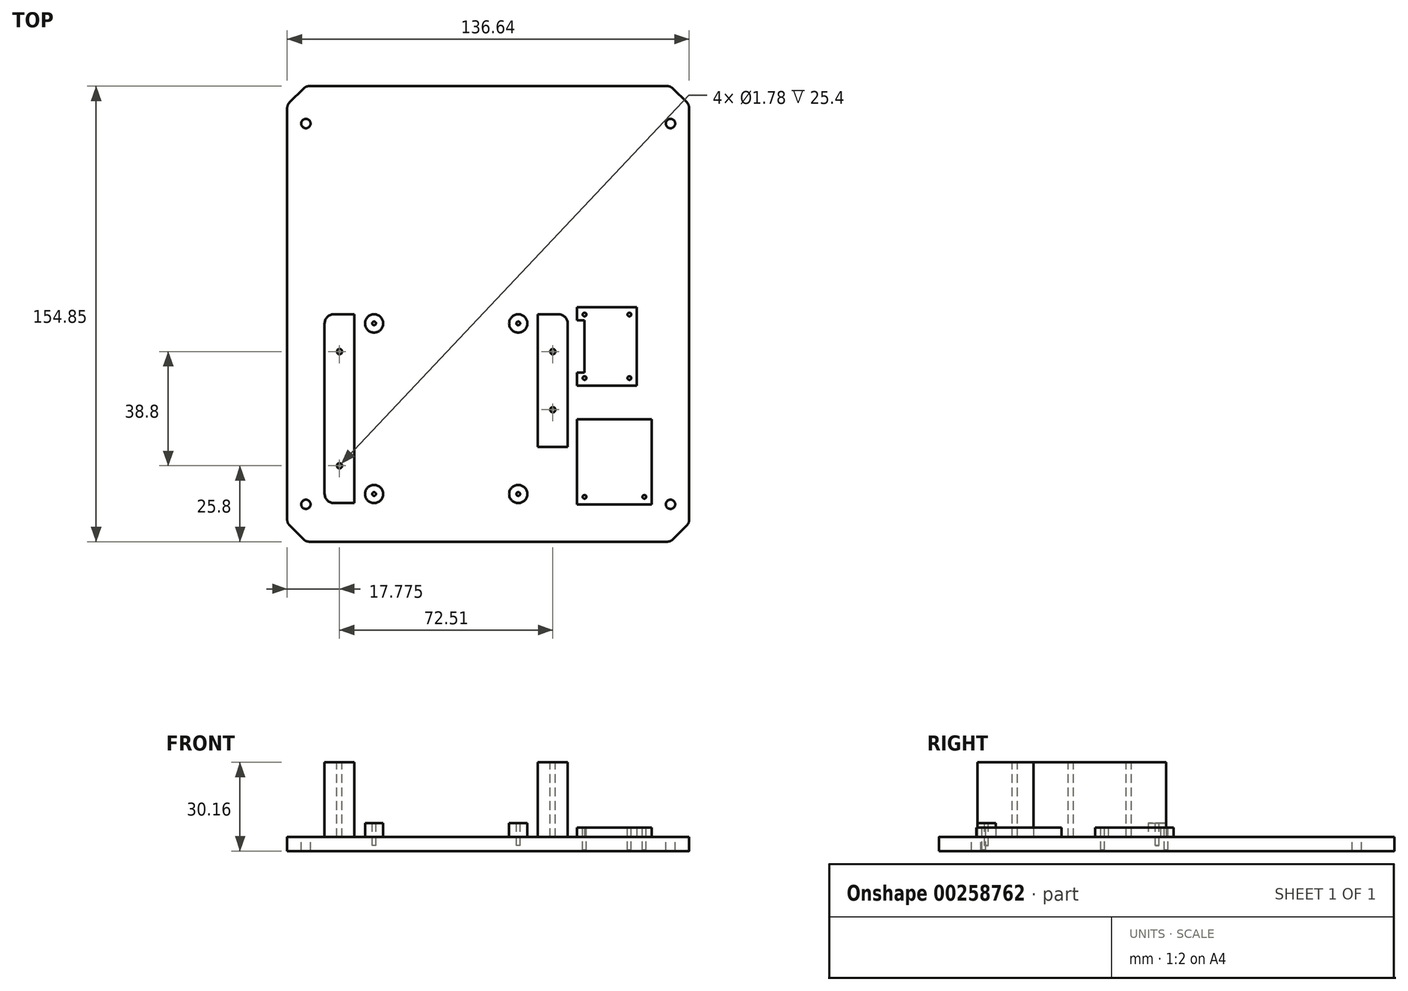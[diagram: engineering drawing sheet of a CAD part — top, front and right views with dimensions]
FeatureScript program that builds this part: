
annotation { "Feature Type Name" : "Feature", "Feature Type Description" : "" }
export const myFeature = defineFeature(function(context is Context, id is Id, definition is map)
    precondition{}
    {
        {
            var Q0;
            Q0=qCreatedBy(makeId("Top.planeOp"),FACE);
            var sketch = newSketch(context, id + "F0", { "sketchPlane" : qUnion([Q0])});
            skLineSegment(sketch, "E0.bottom", {"start": v(-25, 46.5) * mm, "end": v(25, 46.5) * mm});
            skLineSegment(sketch, "E0.top", {"start": v(-25, -38.5) * mm, "end": v(25, -38.5) * mm});
            skLineSegment(sketch, "E0.left", {"start": v(-28, 43.5) * mm, "end": v(-28, -35.5) * mm});
            skLineSegment(sketch, "E0.right", {"start": v(28, 43.5) * mm, "end": v(28, -35.5) * mm});
            skCircle(sketch, "E1", {"center": v(-24.5, -35) * mm, "radius": 3.1 * mm});
            skCircle(sketch, "E2", {"center": v(24.5, -35) * mm, "radius": 3.1 * mm});
            skCircle(sketch, "E3", {"center": v(24.5, 23) * mm, "radius": 3.1 * mm});
            skCircle(sketch, "E4", {"center": v(-24.5, 23) * mm, "radius": 3.1 * mm});
            skCircle(sketch, "E5", {"center": v(-24.5, 23) * mm, "radius": 1.38 * mm});
            skCircle(sketch, "E6", {"center": v(24.5, 23) * mm, "radius": 1.38 * mm});
            skCircle(sketch, "E7", {"center": v(24.5, -35) * mm, "radius": 1.38 * mm});
            skCircle(sketch, "E8", {"center": v(-24.5, -35) * mm, "radius": 1.38 * mm});
            skPoint(sketch, "E9.visualSharp", {"position": v(-28, 46.5) * mm});
            skArc(sketch, "E9.filletArc", {"start": v(-25, 46.5) * mm, "mid": v(-27.12, 45.62) * mm, "end": v(-28, 43.5) * mm});
            skPoint(sketch, "E10.visualSharp", {"position": v(28, 46.5) * mm});
            skArc(sketch, "E10.filletArc", {"start": v(28, 43.5) * mm, "mid": v(27.12, 45.62) * mm, "end": v(25, 46.5) * mm});
            skPoint(sketch, "E11.visualSharp", {"position": v(-28, -38.5) * mm});
            skArc(sketch, "E11.filletArc", {"start": v(-28, -35.5) * mm, "mid": v(-27.12, -37.62) * mm, "end": v(-25, -38.5) * mm});
            skPoint(sketch, "E12.visualSharp", {"position": v(28, -38.5) * mm});
            skArc(sketch, "E12.filletArc", {"start": v(25, -38.5) * mm, "mid": v(27.12, -37.62) * mm, "end": v(28, -35.5) * mm});
            skSolve(sketch);
        }
        {
            var Q0;
            Q0=qCreatedBy(makeId("Top.planeOp"),FACE);
            var sketch = newSketch(context, id + "F1", { "sketchPlane" : qUnion([Q0])});
            skLineSegment(sketch, "E13.top", {"start": v(-38.16, -38.1) * mm, "end": v(-34.35, -38.1) * mm});
            skLineSegment(sketch, "E13.left", {"start": v(-41.33, 22.92) * mm, "end": v(-41.33, -34.92) * mm});
            skLineSegment(sketch, "E13.right", {"start": v(-31.17, 22.92) * mm, "end": v(-31.17, -34.92) * mm});
            skLineSegment(sketch, "E14.left", {"start": v(31.18, 22.92) * mm, "end": v(31.18, -19.05) * mm});
            skLineSegment(sketch, "E14.right", {"start": v(41.33, 22.92) * mm, "end": v(41.33, -19.05) * mm});
            skPoint(sketch, "E15.visualSharp", {"position": v(-41.33, 26.1) * mm});
            skArc(sketch, "E15.filletArc", {"start": v(-38.16, 26.1) * mm, "mid": v(-40.4, 25.17) * mm, "end": v(-41.33, 22.92) * mm});
            skPoint(sketch, "E16.visualSharp", {"position": v(-31.17, 26.1) * mm});
            skPoint(sketch, "E17.visualSharp", {"position": v(-41.33, -38.1) * mm});
            skArc(sketch, "E17.filletArc", {"start": v(-41.33, -34.92) * mm, "mid": v(-40.4, -37.17) * mm, "end": v(-38.16, -38.1) * mm});
            skPoint(sketch, "E18.visualSharp", {"position": v(-31.17, -38.1) * mm});
            skPoint(sketch, "E19.visualSharp", {"position": v(31.18, 26.1) * mm});
            skPoint(sketch, "E20.visualSharp", {"position": v(41.33, 26.1) * mm});
            skArc(sketch, "E20.filletArc", {"start": v(41.33, 22.92) * mm, "mid": v(40.4, 25.17) * mm, "end": v(38.16, 26.1) * mm});
            skPoint(sketch, "E21.visualSharp", {"position": v(31.18, -38.1) * mm});
            skPoint(sketch, "E22.visualSharp", {"position": v(41.33, -38.1) * mm});
            skLineSegment(sketch, "E23", {"start": v(31.18, -19.05) * mm, "end": v(41.34, -19.05) * mm});
            skLineSegment(sketch, "E24", {"start": v(-31.17, 22.92) * mm, "end": v(-31.17, 26.1) * mm});
            skLineSegment(sketch, "E25", {"start": v(-34.35, -38.1) * mm, "end": v(-31.17, -38.1) * mm});
            skLineSegment(sketch, "E26", {"start": v(-31.17, -34.92) * mm, "end": v(-31.17, -38.1) * mm});
            skLineSegment(sketch, "E27", {"start": v(31.18, 22.92) * mm, "end": v(31.18, 26.1) * mm});
            skLineSegment(sketch, "E28", {"start": v(-38.16, 26.1) * mm, "end": v(-31.17, 26.1) * mm});
            skLineSegment(sketch, "E29", {"start": v(31.18, 26.1) * mm, "end": v(38.16, 26.1) * mm});
            skSolve(sketch);
        }
        {
            var Q0;
            Q0=qCreatedBy(makeId("Top.planeOp"),FACE);
            var sketch = newSketch(context, id + "F2", { "sketchPlane" : qUnion([Q0])});
            skLineSegment(sketch, "E30.bottom", {"start": v(44.5, -4.46) * mm, "end": v(69.9, -4.46) * mm});
            skLineSegment(sketch, "E30.top", {"start": v(44.5, -38.5) * mm, "end": v(69.9, -38.5) * mm});
            skLineSegment(sketch, "E30.left", {"start": v(44.5, -4.46) * mm, "end": v(44.5, -38.5) * mm});
            skLineSegment(sketch, "E30.right", {"start": v(69.9, -4.46) * mm, "end": v(69.9, -38.5) * mm});
            skCircle(sketch, "E31", {"center": v(47.05, -35.96) * mm, "radius": 1.14 * mm});
            skCircle(sketch, "E32", {"center": v(67.37, -35.96) * mm, "radius": 1.14 * mm});
            skLineSegment(sketch, "E33", {"start": v(44.5, -9.54) * mm, "end": v(69.9, -9.54) * mm});
            skSolve(sketch);
        }
        {
            var Q0;
            Q0=qCreatedBy(makeId("Top.planeOp"),FACE);
            var sketch = newSketch(context, id + "F3", { "sketchPlane" : qUnion([Q0])});
            skLineSegment(sketch, "E34.bottom", {"start": v(44.5, 28.56) * mm, "end": v(64.83, 28.56) * mm});
            skLineSegment(sketch, "E34.top", {"start": v(44.5, 1.89) * mm, "end": v(64.83, 1.89) * mm});
            skLineSegment(sketch, "E34.left", {"start": v(44.5, 28.56) * mm, "end": v(44.5, 1.89) * mm});
            skLineSegment(sketch, "E34.right", {"start": v(64.83, 28.56) * mm, "end": v(64.83, 1.89) * mm});
            skCircle(sketch, "E35", {"center": v(47.05, 26.02) * mm, "radius": 1.14 * mm});
            skCircle(sketch, "E36", {"center": v(62.3, 26.02) * mm, "radius": 1.14 * mm});
            skCircle(sketch, "E37", {"center": v(62.3, 4.43) * mm, "radius": 1.14 * mm});
            skCircle(sketch, "E38", {"center": v(47.05, 4.43) * mm, "radius": 1.14 * mm});
            skLineSegment(sketch, "E39.bottom", {"start": v(47.05, 24.11) * mm, "end": v(44.5, 24.11) * mm});
            skLineSegment(sketch, "E39.top", {"start": v(47.05, 6.33) * mm, "end": v(44.5, 6.33) * mm});
            skLineSegment(sketch, "E39.left", {"start": v(47.05, 24.11) * mm, "end": v(47.05, 6.33) * mm});
            skLineSegment(sketch, "E39.right", {"start": v(44.5, 24.11) * mm, "end": v(44.5, 6.33) * mm});
            skSolve(sketch);
        }
        {
            var Q0;
            Q0=qCreatedBy(makeId("Top.planeOp"),FACE);
            var sketch = newSketch(context, id + "F4", { "sketchPlane" : qUnion([Q0])});
            skLineSegment(sketch, "E40.bottom", {"start": v(-54.03, 103.65) * mm, "end": v(82.61, 103.65) * mm});
            skLineSegment(sketch, "E40.top", {"start": v(-54.03, -51.2) * mm, "end": v(82.61, -51.2) * mm});
            skLineSegment(sketch, "E40.left", {"start": v(-54.03, 103.65) * mm, "end": v(-54.03, -51.2) * mm});
            skLineSegment(sketch, "E40.right", {"start": v(82.61, 103.65) * mm, "end": v(82.61, -51.2) * mm});
            skSolve(sketch);
        }
        {
            var Q0;
            Q0=makeQuery(id+"F4.imprint","IMPRINT",FACE,{"disambiguationData":[TD([[makeQuery(id+"F4.imprint","IMPRINT",EDGE,{"derivedFrom":sQuery(id+"F4.wireOp",EDGE,"E40.bottom")}),-1.0]])]});
            extrude(context, id + "F5", {"entities" : qUnion([Q0]), "oppositeDirection" : true, "depth" : 4.76 * mm});
        }
        {
            var Q0;
            Q0=makeQuery(id+"F0.imprint","IMPRINT",FACE,{"disambiguationData":[TD([[makeQuery(id+"F0.imprint","IMPRINT",EDGE,{"derivedFrom":sQuery(id+"F0.wireOp",EDGE,"E4")}),1.0]])]});
            var Q1;
            Q1=makeQuery(id+"F0.imprint","IMPRINT",FACE,{"disambiguationData":[TD([[makeQuery(id+"F0.imprint","IMPRINT",EDGE,{"derivedFrom":sQuery(id+"F0.wireOp",EDGE,"E5")}),1.0]])]});
            var Q2;
            Q2=makeQuery(id+"F0.imprint","IMPRINT",FACE,{"disambiguationData":[TD([[makeQuery(id+"F0.imprint","IMPRINT",EDGE,{"derivedFrom":sQuery(id+"F0.wireOp",EDGE,"E6")}),1.0]])]});
            var Q3;
            Q3=makeQuery(id+"F0.imprint","IMPRINT",FACE,{"disambiguationData":[TD([[makeQuery(id+"F0.imprint","IMPRINT",EDGE,{"derivedFrom":sQuery(id+"F0.wireOp",EDGE,"E3")}),1.0]])]});
            var Q4;
            Q4=makeQuery(id+"F0.imprint","IMPRINT",FACE,{"disambiguationData":[TD([[makeQuery(id+"F0.imprint","IMPRINT",EDGE,{"derivedFrom":sQuery(id+"F0.wireOp",EDGE,"E8")}),1.0]])]});
            var Q5;
            Q5=makeQuery(id+"F0.imprint","IMPRINT",FACE,{"disambiguationData":[TD([[makeQuery(id+"F0.imprint","IMPRINT",EDGE,{"derivedFrom":sQuery(id+"F0.wireOp",EDGE,"E1")}),1.0]])]});
            var Q6;
            Q6=makeQuery(id+"F0.imprint","IMPRINT",FACE,{"disambiguationData":[TD([[makeQuery(id+"F0.imprint","IMPRINT",EDGE,{"derivedFrom":sQuery(id+"F0.wireOp",EDGE,"E7")}),1.0]])]});
            var Q7;
            Q7=makeQuery(id+"F0.imprint","IMPRINT",FACE,{"disambiguationData":[TD([[makeQuery(id+"F0.imprint","IMPRINT",EDGE,{"derivedFrom":sQuery(id+"F0.wireOp",EDGE,"E2")}),1.0]])]});
            extrude(context, id + "F6", {"entities" : qUnion([Q0, Q1, Q2, Q3, Q4, Q5, Q6, Q7]), "operationType" : NewBodyOperationType.ADD, "depth" : 4.76 * mm});
        }
        {
            var Q0;
            Q0=makeQuery(id+"F1.imprint","IMPRINT",FACE,{"disambiguationData":[TD([[makeQuery(id+"F1.imprint","IMPRINT",EDGE,{"derivedFrom":sQuery(id+"F1.wireOp",EDGE,"E14.bottom")}),-1.0]])]});
            var Q1;
            Q1=makeQuery(id+"F1.imprint","IMPRINT",FACE,{"disambiguationData":[TD([[makeQuery(id+"F1.imprint","IMPRINT",EDGE,{"derivedFrom":sQuery(id+"F1.wireOp",EDGE,"E13.bottom")}),-1.0]])]});
            var Q2;
            Q2=makeQuery(id+"F1.imprint","IMPRINT",FACE,{"disambiguationData":[TD([[makeQuery(id+"F1.imprint","IMPRINT",EDGE,{"derivedFrom":sQuery(id+"F1.wireOp",EDGE,"E13.top")}),1.0]])]});
            var Q3;
            Q3=makeQuery(id+"F1.imprint","IMPRINT",FACE,{"disambiguationData":[TD([[makeQuery(id+"F1.imprint","IMPRINT",EDGE,{"derivedFrom":sQuery(id+"F1.wireOp",EDGE,"E14.left")}),1.0]])]});
            extrude(context, id + "F7", {"entities" : qUnion([Q0, Q1, Q2, Q3]), "operationType" : NewBodyOperationType.ADD, "depth" : 25.4 * mm});
        }
        {
            var Q0;
            Q0=makeQuery(id+"F3.imprint","IMPRINT",FACE,{"disambiguationData":[TD([[makeQuery(id+"F3.imprint","IMPRINT",EDGE,{"derivedFrom":sQuery(id+"F3.wireOp",EDGE,"E37")}),1.0]])]});
            var Q1;
            Q1=makeQuery(id+"F3.imprint","IMPRINT",FACE,{"disambiguationData":[TD([[makeQuery(id+"F3.imprint","IMPRINT",EDGE,{"derivedFrom":sQuery(id+"F3.wireOp",EDGE,"E36")}),1.0]])]});
            var Q2;
            Q2=makeQuery(id+"F3.imprint","IMPRINT",FACE,{"disambiguationData":[TD([[makeQuery(id+"F3.imprint","IMPRINT",EDGE,{"derivedFrom":sQuery(id+"F3.wireOp",EDGE,"E35")}),1.0]])]});
            var Q3;
            Q3=makeQuery(id+"F3.imprint","IMPRINT",FACE,{"disambiguationData":[TD([[makeQuery(id+"F3.imprint","IMPRINT",EDGE,{"derivedFrom":sQuery(id+"F3.wireOp",EDGE,"E38")}),1.0]])]});
            var Q4;
            {var subQ0=sQuery(id+"F3.wireOp",EDGE,"E34.bottom");Q4=makeQuery(id+"F3.imprint","IMPRINT",FACE,{"disambiguationData":[TD([[makeQuery(id+"F3.imprint","IMPRINT",EDGE,{"derivedFrom":subQ0}),-1.0]])]});}
            extrude(context, id + "F8", {"entities" : qUnion([Q0, Q1, Q2, Q3, Q4]), "operationType" : NewBodyOperationType.ADD, "depth" : 3.17 * mm});
        }
        {
            var Q0;
            Q0=makeQuery(id+"F2.imprint","IMPRINT",FACE,{"disambiguationData":[TD([[makeQuery(id+"F2.imprint","IMPRINT",EDGE,{"derivedFrom":sQuery(id+"F2.wireOp",EDGE,"E31")}),1.0]])]});
            var Q1;
            Q1=makeQuery(id+"F2.imprint","IMPRINT",FACE,{"disambiguationData":[TD([[makeQuery(id+"F2.imprint","IMPRINT",EDGE,{"derivedFrom":sQuery(id+"F2.wireOp",EDGE,"E32")}),1.0]])]});
            var Q2;
            {var subQ1=sQuery(id+"F2.wireOp",EDGE,"E30.top");Q2=makeQuery(id+"F2.imprint","IMPRINT",FACE,{"disambiguationData":[TD([[makeQuery(id+"F2.imprint","IMPRINT",EDGE,{"derivedFrom":subQ1}),1.0]])]});}
            extrude(context, id + "F9", {"entities" : qUnion([Q0, Q1, Q2]), "operationType" : NewBodyOperationType.ADD, "depth" : 3.17 * mm});
        }
        {
            var Q0;
            Q0=makeQuery(id+"F8.opExtrude","CAP_FACE",FACE,{"disambiguationData":[OSD([sQuery(id+"F3.wireOp",EDGE,"E34.bottom"),sQuery(id+"F3.wireOp",EDGE,"E34.top"),sQuery(id+"F3.wireOp",EDGE,"E34.left"),sQuery(id+"F3.wireOp",EDGE,"E34.right"),sQuery(id+"F3.wireOp",EDGE,"E39.bottom"),sQuery(id+"F3.wireOp",EDGE,"E39.top"),sQuery(id+"F3.wireOp",EDGE,"E39.left")])],"isStart":false});
            var sketch = newSketch(context, id + "F10", { "sketchPlane" : qUnion([Q0])});
            skCircle(sketch, "E41", {"center": v(47.05, 26.02) * mm, "radius": 0.64 * mm});
            skCircle(sketch, "E42", {"center": v(62.3, 26.02) * mm, "radius": 0.64 * mm});
            skCircle(sketch, "E43", {"center": v(62.3, 4.43) * mm, "radius": 0.64 * mm});
            skCircle(sketch, "E44", {"center": v(47.05, 4.43) * mm, "radius": 0.64 * mm});
            skCircle(sketch, "E45", {"center": v(47.05, -35.96) * mm, "radius": 0.64 * mm});
            skCircle(sketch, "E46", {"center": v(67.37, -35.96) * mm, "radius": 0.64 * mm});
            skSolve(sketch);
        }
        {
            var Q0;
            Q0 = qSketchRegion(id + "F10", true);
            extrude(context, id + "F11", {"entities" : qUnion([Q0]), "operationType" : NewBodyOperationType.REMOVE, "oppositeDirection" : true, "depth" : 7.62 * mm});
        }
        {
            var Q0;
            Q0=makeQuery(id+"F6.opExtrude","CAP_FACE",FACE,{"disambiguationData":[OSD([sQuery(id+"F0.wireOp",EDGE,"E4")])],"isStart":false});
            var sketch = newSketch(context, id + "F12", { "sketchPlane" : qUnion([Q0])});
            skCircle(sketch, "E47", {"center": v(-24.5, 23) * mm, "radius": 0.64 * mm});
            skCircle(sketch, "E48", {"center": v(24.5, 23) * mm, "radius": 0.64 * mm});
            skCircle(sketch, "E49", {"center": v(24.5, -35) * mm, "radius": 0.64 * mm});
            skCircle(sketch, "E50", {"center": v(-24.5, -35) * mm, "radius": 0.64 * mm});
            skSolve(sketch);
        }
        {
            var Q0;
            Q0=makeQuery(id+"F7.opExtrude","CAP_FACE",FACE,{"disambiguationData":[OSD([sQuery(id+"F1.wireOp",EDGE,"E13.top"),sQuery(id+"F1.wireOp",EDGE,"E13.left"),sQuery(id+"F1.wireOp",EDGE,"E13.right"),sQuery(id+"F1.wireOp",EDGE,"E15.filletArc"),sQuery(id+"F1.wireOp",EDGE,"E17.filletArc"),sQuery(id+"F1.wireOp",EDGE,"E24"),sQuery(id+"F1.wireOp",EDGE,"E25"),sQuery(id+"F1.wireOp",EDGE,"E26"),sQuery(id+"F1.wireOp",EDGE,"E28")])],"isStart":false});
            var sketch = newSketch(context, id + "F13", { "sketchPlane" : qUnion([Q0])});
            skSolve(sketch);
        }
        {
            var Q0;
            Q0=makeQuery(id+"F12.imprint","IMPRINT",FACE,{"disambiguationData":[TD([[makeQuery(id+"F12.imprint","IMPRINT",EDGE,{"derivedFrom":sQuery(id+"F12.wireOp",EDGE,"E47")}),1.0]])]});
            var Q1;
            Q1=makeQuery(id+"F12.imprint","IMPRINT",FACE,{"disambiguationData":[TD([[makeQuery(id+"F12.imprint","IMPRINT",EDGE,{"derivedFrom":sQuery(id+"F12.wireOp",EDGE,"E48")}),1.0]])]});
            var Q2;
            Q2=makeQuery(id+"F12.imprint","IMPRINT",FACE,{"disambiguationData":[TD([[makeQuery(id+"F12.imprint","IMPRINT",EDGE,{"derivedFrom":sQuery(id+"F12.wireOp",EDGE,"E49")}),1.0]])]});
            var Q3;
            Q3=makeQuery(id+"F12.imprint","IMPRINT",FACE,{"disambiguationData":[TD([[makeQuery(id+"F12.imprint","IMPRINT",EDGE,{"derivedFrom":sQuery(id+"F12.wireOp",EDGE,"E50")}),1.0]])]});
            extrude(context, id + "F14", {"entities" : qUnion([Q0, Q1, Q2, Q3]), "operationType" : NewBodyOperationType.REMOVE, "oppositeDirection" : true, "depth" : 7.62 * mm});
        }
        {
            var Q0;
            Q0=makeQuery(id+"F13.imprint","IMPRINT",FACE,{"disambiguationData":[TD([[makeQuery(id+"F13.imprint","IMPRINT",EDGE,{"derivedFrom":makeQuery(id+"F7.opExtrude","CAP_EDGE",EDGE,{"disambiguationData":[OSD([sQuery(id+"F1.wireOp",EDGE,"E13.left")])],"isStart":false})}),1.0]])]});
            var sketch = newSketch(context, id + "F15", { "sketchPlane" : qUnion([Q0])});
            skCircle(sketch, "E51", {"center": v(-36.25, 13.4) * mm, "radius": 0.89 * mm});
            skCircle(sketch, "E52", {"center": v(36.26, 13.4) * mm, "radius": 0.89 * mm});
            skCircle(sketch, "E53", {"center": v(36.26, -6.35) * mm, "radius": 0.89 * mm});
            skCircle(sketch, "E54", {"center": v(-36.25, -25.4) * mm, "radius": 0.89 * mm});
            skSolve(sketch);
        }
        {
            var Q0;
            Q0=makeQuery(id+"F15.imprint","IMPRINT",FACE,{"disambiguationData":[TD([[makeQuery(id+"F15.imprint","IMPRINT",EDGE,{"derivedFrom":sQuery(id+"F15.wireOp",EDGE,"E51")}),1.0]])]});
            var Q1;
            Q1=makeQuery(id+"F15.imprint","IMPRINT",FACE,{"disambiguationData":[TD([[makeQuery(id+"F15.imprint","IMPRINT",EDGE,{"derivedFrom":sQuery(id+"F15.wireOp",EDGE,"E53")}),1.0]])]});
            var Q2;
            Q2=makeQuery(id+"F15.imprint","IMPRINT",FACE,{"disambiguationData":[TD([[makeQuery(id+"F15.imprint","IMPRINT",EDGE,{"derivedFrom":sQuery(id+"F15.wireOp",EDGE,"E52")}),1.0]])]});
            var Q3;
            Q3=makeQuery(id+"F15.imprint","IMPRINT",FACE,{"disambiguationData":[TD([[makeQuery(id+"F15.imprint","IMPRINT",EDGE,{"derivedFrom":sQuery(id+"F15.wireOp",EDGE,"E54")}),1.0]])]});
            extrude(context, id + "F16", {"entities" : qUnion([Q0, Q1, Q2, Q3]), "operationType" : NewBodyOperationType.REMOVE, "oppositeDirection" : true, "depth" : 25.4 * mm});
        }
        {
            var Q0;
            Q0=makeQuery(id+"F5.opExtrude","SWEPT_EDGE",EDGE,{"disambiguationData":[OSD([sQuery(id+"F4.wireOp",EDGE,"E40.bottom"),sQuery(id+"F4.wireOp",EDGE,"E40.left")])]});
            var Q1;
            Q1=makeQuery(id+"F5.opExtrude","SWEPT_EDGE",EDGE,{"disambiguationData":[OSD([sQuery(id+"F4.wireOp",EDGE,"E40.bottom"),sQuery(id+"F4.wireOp",EDGE,"E40.right")])]});
            var Q2;
            Q2=makeQuery(id+"F5.opExtrude","SWEPT_EDGE",EDGE,{"disambiguationData":[OSD([sQuery(id+"F4.wireOp",EDGE,"E40.top"),sQuery(id+"F4.wireOp",EDGE,"E40.right")])]});
            var Q3;
            Q3=makeQuery(id+"F5.opExtrude","SWEPT_EDGE",EDGE,{"disambiguationData":[OSD([sQuery(id+"F4.wireOp",EDGE,"E40.top"),sQuery(id+"F4.wireOp",EDGE,"E40.left")])]});
            chamfer(context, id + "F17", {"entities" : qUnion([Q0, Q1, Q2, Q3]), "width" : 6.35 * mm, "tangentPropagation" : true});
        }
        {
            var Q0;
            {var subQ0=sQuery(id+"F4.wireOp",EDGE,"E40.right");Q0=makeQuery(id+"F17.opChamfer","BLEND_EDGE",EDGE,{"blendedFrom":[makeQuery(id+"F5.opExtrude","SWEPT_EDGE",EDGE,{"disambiguationData":[OSD([sQuery(id+"F4.wireOp",EDGE,"E40.bottom"),subQ0])]}),makeQuery(id+"F5.opExtrude","SWEPT_FACE",FACE,{"disambiguationData":[OSD([subQ0])]})],"blendedInto":[makeQuery(id+"F5.opExtrude","SWEPT_FACE",FACE,{"disambiguationData":[OSD([subQ0])]})]});}
            var Q1;
            {var subQ0=sQuery(id+"F4.wireOp",EDGE,"E40.bottom");Q1=makeQuery(id+"F17.opChamfer","BLEND_EDGE",EDGE,{"blendedFrom":[makeQuery(id+"F5.opExtrude","SWEPT_EDGE",EDGE,{"disambiguationData":[OSD([subQ0,sQuery(id+"F4.wireOp",EDGE,"E40.right")])]}),makeQuery(id+"F5.opExtrude","SWEPT_FACE",FACE,{"disambiguationData":[OSD([subQ0])]})],"blendedInto":[makeQuery(id+"F5.opExtrude","SWEPT_FACE",FACE,{"disambiguationData":[OSD([subQ0])]})]});}
            var Q2;
            {var subQ0=sQuery(id+"F4.wireOp",EDGE,"E40.bottom");Q2=makeQuery(id+"F17.opChamfer","BLEND_EDGE",EDGE,{"blendedFrom":[makeQuery(id+"F5.opExtrude","SWEPT_EDGE",EDGE,{"disambiguationData":[OSD([subQ0,sQuery(id+"F4.wireOp",EDGE,"E40.left")])]}),makeQuery(id+"F5.opExtrude","SWEPT_FACE",FACE,{"disambiguationData":[OSD([subQ0])]})],"blendedInto":[makeQuery(id+"F5.opExtrude","SWEPT_FACE",FACE,{"disambiguationData":[OSD([subQ0])]})]});}
            var Q3;
            {var subQ0=sQuery(id+"F4.wireOp",EDGE,"E40.left");Q3=makeQuery(id+"F17.opChamfer","BLEND_EDGE",EDGE,{"blendedFrom":[makeQuery(id+"F5.opExtrude","SWEPT_EDGE",EDGE,{"disambiguationData":[OSD([sQuery(id+"F4.wireOp",EDGE,"E40.bottom"),subQ0])]}),makeQuery(id+"F5.opExtrude","SWEPT_FACE",FACE,{"disambiguationData":[OSD([subQ0])]})],"blendedInto":[makeQuery(id+"F5.opExtrude","SWEPT_FACE",FACE,{"disambiguationData":[OSD([subQ0])]})]});}
            var Q4;
            {var subQ0=sQuery(id+"F4.wireOp",EDGE,"E40.left");Q4=makeQuery(id+"F17.opChamfer","BLEND_EDGE",EDGE,{"blendedFrom":[makeQuery(id+"F5.opExtrude","SWEPT_EDGE",EDGE,{"disambiguationData":[OSD([sQuery(id+"F4.wireOp",EDGE,"E40.top"),subQ0])]}),makeQuery(id+"F5.opExtrude","SWEPT_FACE",FACE,{"disambiguationData":[OSD([subQ0])]})],"blendedInto":[makeQuery(id+"F5.opExtrude","SWEPT_FACE",FACE,{"disambiguationData":[OSD([subQ0])]})]});}
            var Q5;
            {var subQ0=sQuery(id+"F4.wireOp",EDGE,"E40.top");Q5=makeQuery(id+"F17.opChamfer","BLEND_EDGE",EDGE,{"blendedFrom":[makeQuery(id+"F5.opExtrude","SWEPT_EDGE",EDGE,{"disambiguationData":[OSD([subQ0,sQuery(id+"F4.wireOp",EDGE,"E40.left")])]}),makeQuery(id+"F5.opExtrude","SWEPT_FACE",FACE,{"disambiguationData":[OSD([subQ0])]})],"blendedInto":[makeQuery(id+"F5.opExtrude","SWEPT_FACE",FACE,{"disambiguationData":[OSD([subQ0])]})]});}
            var Q6;
            {var subQ0=sQuery(id+"F4.wireOp",EDGE,"E40.top");Q6=makeQuery(id+"F17.opChamfer","BLEND_EDGE",EDGE,{"blendedFrom":[makeQuery(id+"F5.opExtrude","SWEPT_EDGE",EDGE,{"disambiguationData":[OSD([subQ0,sQuery(id+"F4.wireOp",EDGE,"E40.right")])]}),makeQuery(id+"F5.opExtrude","SWEPT_FACE",FACE,{"disambiguationData":[OSD([subQ0])]})],"blendedInto":[makeQuery(id+"F5.opExtrude","SWEPT_FACE",FACE,{"disambiguationData":[OSD([subQ0])]})]});}
            var Q7;
            {var subQ0=sQuery(id+"F4.wireOp",EDGE,"E40.right");Q7=makeQuery(id+"F17.opChamfer","BLEND_EDGE",EDGE,{"blendedFrom":[makeQuery(id+"F5.opExtrude","SWEPT_EDGE",EDGE,{"disambiguationData":[OSD([sQuery(id+"F4.wireOp",EDGE,"E40.top"),subQ0])]}),makeQuery(id+"F5.opExtrude","SWEPT_FACE",FACE,{"disambiguationData":[OSD([subQ0])]})],"blendedInto":[makeQuery(id+"F5.opExtrude","SWEPT_FACE",FACE,{"disambiguationData":[OSD([subQ0])]})]});}
            fillet(context, id + "F18", {"entities" : qUnion([Q0, Q1, Q2, Q3, Q4, Q5, Q6, Q7]), "radius" : 2.54 * mm, "tangentPropagation" : true, "allowEdgeOverflow" : false});
        }
        {
            var Q0;
            Q0=makeQuery(id+"F4.imprint","IMPRINT",FACE,{"disambiguationData":[TD([[makeQuery(id+"F4.imprint","IMPRINT",EDGE,{"derivedFrom":sQuery(id+"F4.wireOp",EDGE,"E40.bottom")}),-1.0]])]});
            var sketch = newSketch(context, id + "F19", { "sketchPlane" : qUnion([Q0])});
            skCircle(sketch, "E55", {"center": v(-47.68, 90.95) * mm, "radius": 1.59 * mm});
            skCircle(sketch, "E56", {"center": v(76.26, 90.95) * mm, "radius": 1.59 * mm});
            skCircle(sketch, "E57", {"center": v(76.26, -38.5) * mm, "radius": 1.59 * mm});
            skCircle(sketch, "E58", {"center": v(-47.68, -38.5) * mm, "radius": 1.59 * mm});
            skSolve(sketch);
        }
        {
            var Q0;
            Q0 = qSketchRegion(id + "F19", true);
            extrude(context, id + "F20", {"entities" : qUnion([Q0]), "operationType" : NewBodyOperationType.REMOVE, "endBound" : BoundingType.THROUGH_ALL, "oppositeDirection" : true, "depth" : 25.4 * mm});
        }
    });
